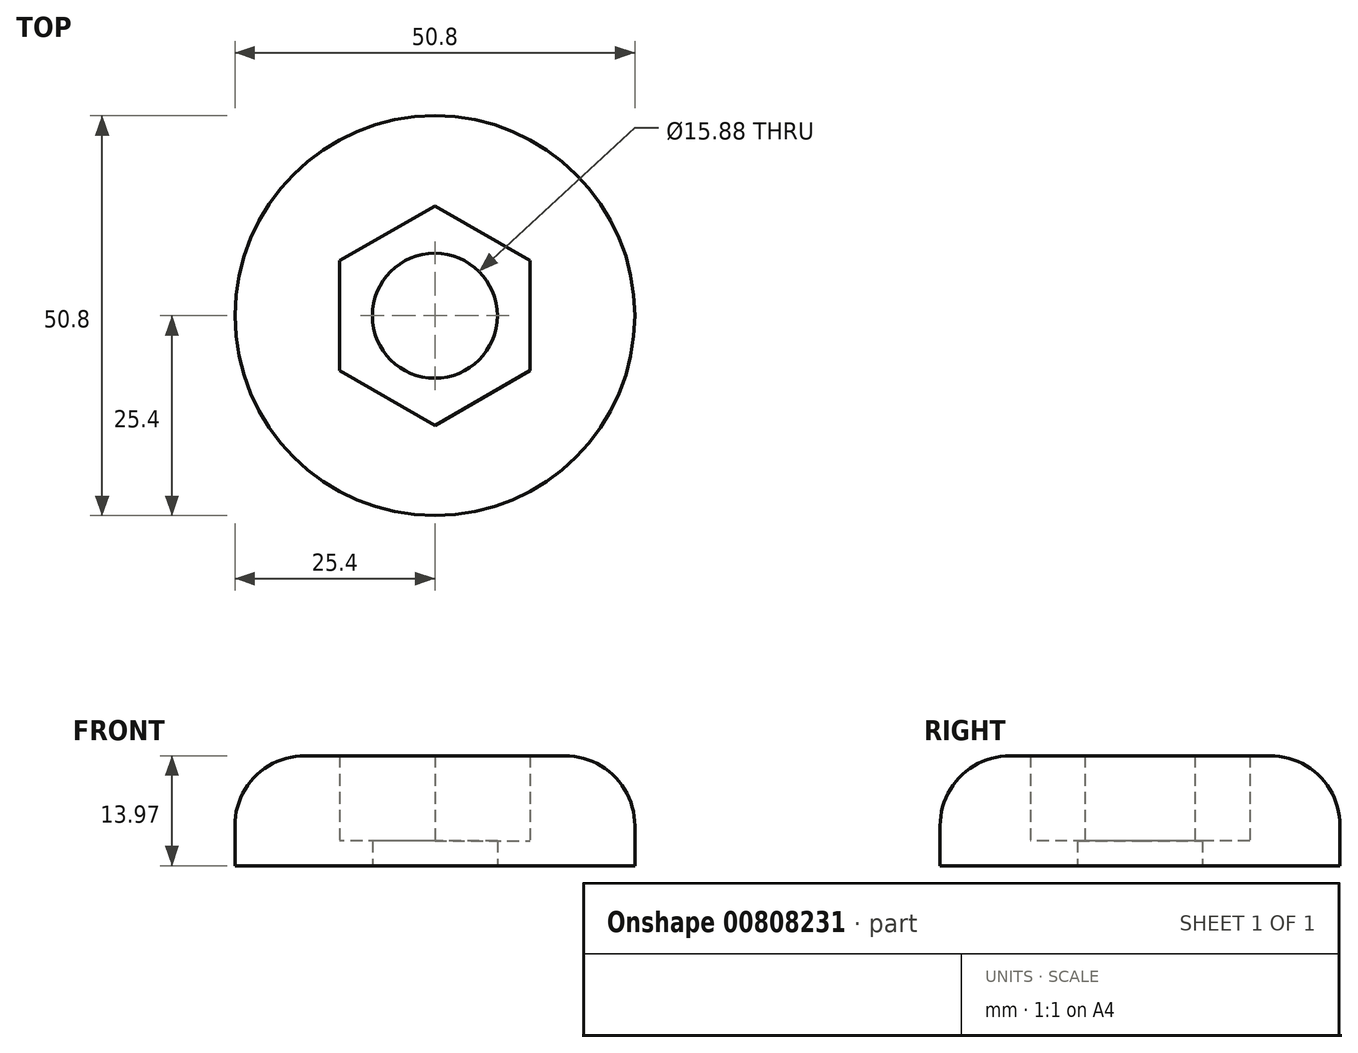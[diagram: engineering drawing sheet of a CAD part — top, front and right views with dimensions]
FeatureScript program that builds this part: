
annotation { "Feature Type Name" : "Feature", "Feature Type Description" : "" }
export const myFeature = defineFeature(function(context is Context, id is Id, definition is map)
    precondition{}
    {
        {
            var Q0;
            Q0=qCreatedBy(makeId("Top.planeOp"),FACE);
            var sketch = newSketch(context, id + "F0", { "sketchPlane" : qUnion([Q0])});
            skCircle(sketch, "E0", {"center": v(0, 0) * mm, "radius": 25.4 * mm});
            skCircle(sketch, "E1", {"center": v(0, 0) * mm, "radius": 7.94 * mm});
            skCircle(sketch, "E2.cCircle", {"center": v(0, 0) * mm, "radius": 12.09 * mm, "construction": true});
            skLineSegment(sketch, "E2.0", {"start": v(12.09, 6.98) * mm, "end": v(12.09, -6.98) * mm});
            skLineSegment(sketch, "E2.1", {"start": v(12.09, -6.98) * mm, "end": v(0, -13.96) * mm});
            skLineSegment(sketch, "E2.2", {"start": v(0, -13.96) * mm, "end": v(-12.09, -6.98) * mm});
            skLineSegment(sketch, "E2.3", {"start": v(-12.09, -6.98) * mm, "end": v(-12.09, 6.98) * mm});
            skLineSegment(sketch, "E2.4", {"start": v(-12.09, 6.98) * mm, "end": v(0, 13.96) * mm});
            skLineSegment(sketch, "E2.5", {"start": v(0, 13.96) * mm, "end": v(12.09, 6.98) * mm});
            skPoint(sketch, "E2.0.midPoint", {"position": v(12.09, 0) * mm});
            skSolve(sketch);
        }
        {
            var Q0;
            Q0=makeQuery(id+"F0.imprint","IMPRINT",FACE,{"disambiguationData":[TD([[makeQuery(id+"F0.imprint","IMPRINT",EDGE,{"derivedFrom":sQuery(id+"F0.wireOp",EDGE,"E0")}),1.0]])]});
            extrude(context, id + "F1", {"entities" : qUnion([Q0]), "depth" : 13.97 * mm, "offsetDistance" : 25.4 * mm});
        }
        {
            var Q0;
            Q0=makeQuery(id+"F0.imprint","IMPRINT",FACE,{"disambiguationData":[TD([[makeQuery(id+"F0.imprint","IMPRINT",EDGE,{"derivedFrom":sQuery(id+"F0.wireOp",EDGE,"E1")}),-1.0]])]});
            extrude(context, id + "F2", {"entities" : qUnion([Q0]), "operationType" : NewBodyOperationType.ADD, "depth" : 3.17 * mm, "offsetDistance" : 25.4 * mm});
        }
        {
            var Q0;
            Q0=makeQuery(id+"F1.opExtrude","CAP_EDGE",EDGE,{"disambiguationData":[OSD([sQuery(id+"F0.wireOp",EDGE,"E0")])],"isStart":false});
            fillet(context, id + "F3", {"entities" : qUnion([Q0]), "radius" : 8.9 * mm, "tangentPropagation" : true, "allowEdgeOverflow" : false});
        }
    });
